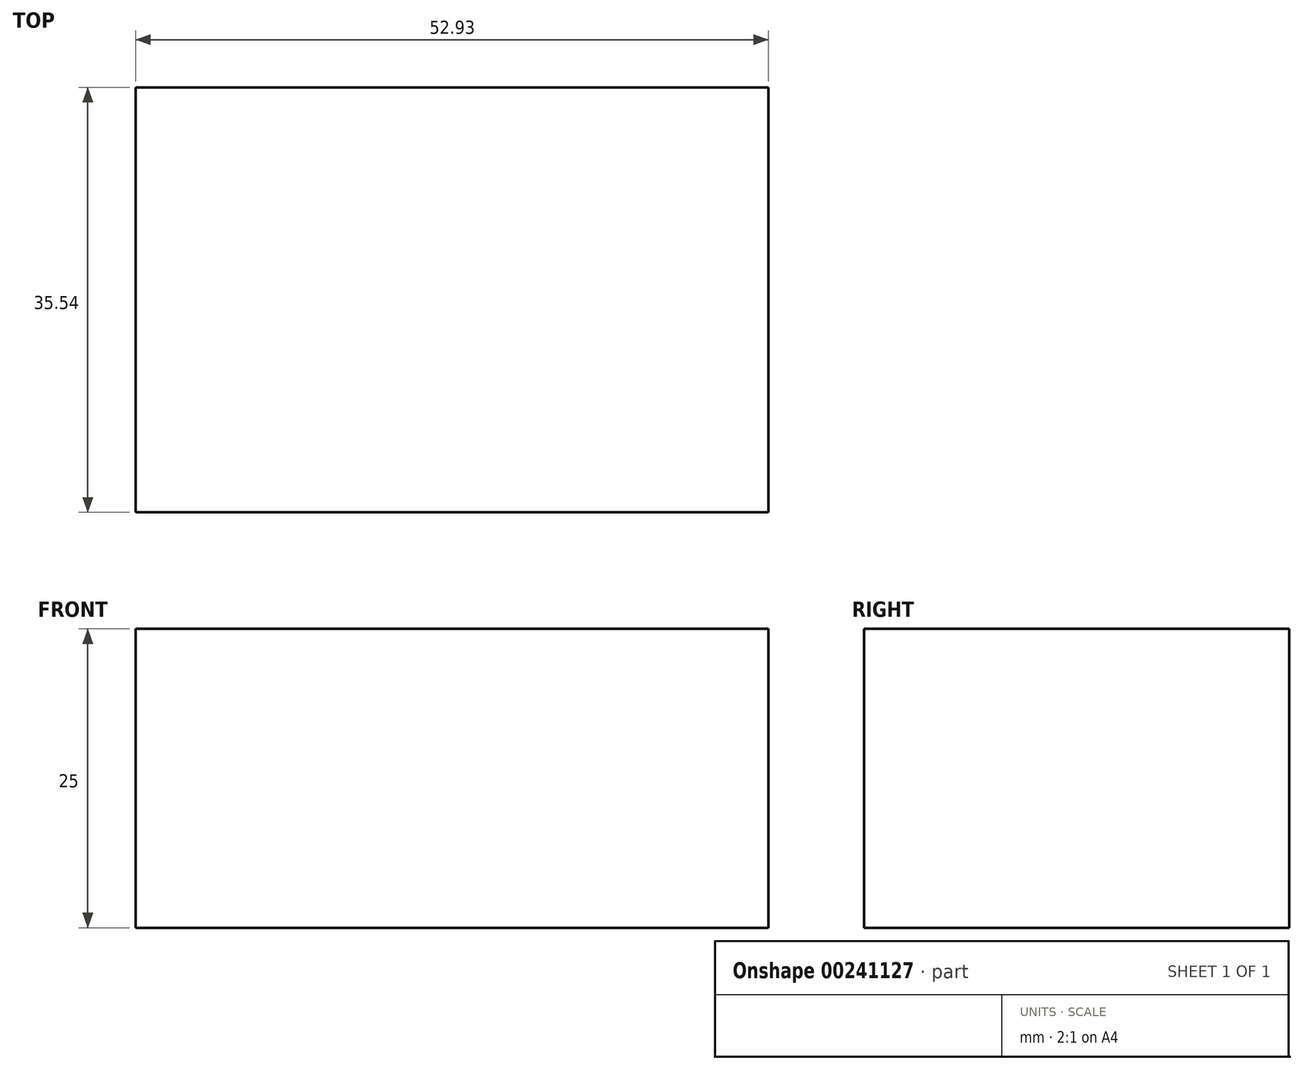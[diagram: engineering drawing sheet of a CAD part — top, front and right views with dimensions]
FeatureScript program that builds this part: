
annotation { "Feature Type Name" : "Feature", "Feature Type Description" : "" }
export const myFeature = defineFeature(function(context is Context, id is Id, definition is map)
    precondition{}
    {
        {
            var Q0;
            Q0=qCreatedBy(makeId("Top.planeOp"),FACE);
            var sketch = newSketch(context, id + "F0", { "sketchPlane" : qUnion([Q0])});
            skLineSegment(sketch, "E0.bottom", {"start": v(0.13, 1.69) * mm, "end": v(53.06, 1.69) * mm});
            skLineSegment(sketch, "E0.top", {"start": v(0.13, 37.23) * mm, "end": v(53.06, 37.23) * mm});
            skLineSegment(sketch, "E0.left", {"start": v(0.13, 1.69) * mm, "end": v(0.13, 37.23) * mm});
            skLineSegment(sketch, "E0.right", {"start": v(53.06, 1.69) * mm, "end": v(53.06, 37.23) * mm});
            skSolve(sketch);
        }
        {
            var Q0;
            Q0=makeQuery(id+"F0.imprint","IMPRINT",FACE,{"disambiguationData":[TD([[makeQuery(id+"F0.imprint","IMPRINT",EDGE,{"derivedFrom":sQuery(id+"F0.wireOp",EDGE,"E0.bottom")}),1.0]])]});
            extrude(context, id + "F1", {"entities" : qUnion([Q0]), "endBound" : BoundingType.SYMMETRIC, "depth" : 25 * mm});
        }
    });
